FCSTD DOCUMENT
Label: SpoolCoaster
objects: Sketcher::SketchObject×1
note: 1 computed .brp shape members not serialized (recipe doc carries the construction recipe); baked Part::Feature solids carry a one-line shape summary decoded from their .brp

FEATURE [Sketcher::SketchObject] Sketch
  sketch-geometry (22):
    g0: Circle [constr] CenterX=0 CenterY=0 CenterZ=0 NormalX=0 NormalY=0 NormalZ=1 Radius=115
    g1: Circle [constr] CenterX=70 CenterY=-110 CenterZ=0 NormalX=0 NormalY=0 NormalZ=1 Radius=15
    g2: LineSegment StartX=-10 StartY=-117.726 StartZ=0 EndX=48.1322 EndY=-117.726 EndZ=0
    g3: LineSegment StartX=48.1322 StartY=-117.726 StartZ=0 EndX=62.9289 EndY=-102.929 EndZ=0
    g4: LineSegment StartX=80 StartY=-110 StartZ=0 EndX=80 EndY=-135 EndZ=0
    g5: ArcOfCircle CenterX=70 CenterY=-110 CenterZ=0 NormalX=0 NormalY=0 NormalZ=1 Radius=10 StartAngle=1.3058e-08 EndAngle=2.35619
    g6: LineSegment StartX=-5 StartY=-123.476 StartZ=0 EndX=60 EndY=-123.476 EndZ=0
    g7: LineSegment StartX=60 StartY=-123.476 StartZ=0 EndX=60 EndY=-126.976 EndZ=0
    g8: LineSegment StartX=60 StartY=-126.976 StartZ=0 EndX=-5 EndY=-126.976 EndZ=0
    g9: LineSegment StartX=-10 StartY=-117.726 StartZ=0 EndX=-10 EndY=-125.226 EndZ=0
    g10: LineSegment StartX=-10 StartY=-125.226 StartZ=0 EndX=-10 EndY=-132.726 EndZ=0
    g11: LineSegment StartX=-5 StartY=-123.476 StartZ=0 EndX=-5 EndY=-125.226 EndZ=0
    g12: LineSegment StartX=-5 StartY=-125.226 StartZ=0 EndX=-5 EndY=-126.976 EndZ=0
    g13: LineSegment [constr] StartX=-10 StartY=-125.226 StartZ=0 EndX=-5 EndY=-125.226 EndZ=0
    g14: Circle CenterX=70 CenterY=-110 CenterZ=0 NormalX=0 NormalY=0 NormalZ=1 Radius=1.8
    g15: Circle CenterX=75 CenterY=-135 CenterZ=0 NormalX=0 NormalY=0 NormalZ=1 Radius=1.8
    g16: LineSegment StartX=-10 StartY=-132.726 StartZ=0 EndX=48.1322 EndY=-132.726 EndZ=0
    g17: LineSegment StartX=48.1322 StartY=-132.726 StartZ=0 EndX=73.6617 EndY=-139.818 EndZ=0
    g18: ArcOfCircle CenterX=75 CenterY=-135 CenterZ=0 NormalX=0 NormalY=0 NormalZ=1 Radius=5 StartAngle=4.44143 EndAngle=6.28319
    g19: LineSegment [constr] StartX=48.1322 StartY=-117.726 StartZ=0 EndX=48.1322 EndY=-132.726 EndZ=0
    g20: Circle CenterX=75 CenterY=-128 CenterZ=0 NormalX=0 NormalY=0 NormalZ=1 Radius=1.8
    g21: LineSegment [constr] StartX=75 StartY=-128 StartZ=0 EndX=75 EndY=-135 EndZ=0
  constraints (64):
    c: DistanceX(g0) = 0
    c: DistanceY(g0) = 0
    c: DistanceX(g0) = 0
    c: DistanceY(g0) = 0
    c: Radius(g0) = 115
    c: DistanceX(g1) = 70
    c: DistanceY(g1) = -110
    c: Radius(g1) = 15
    c: Horizontal(g2)
    c: Coincident(g2,g3)
    c: Vertical(g4)
    c: Coincident(g5,g1)
    c: Coincident(g5,g3)
    c: Coincident(g5,g4)
    c: Tangent(g3,g5)
    c: Tangent(g4,g5)
    c: Radius(g5) = 10
    c: DistanceY(g1,g4) = -25
    c: Horizontal(g6)
    c: Coincident(g6,g7)
    c: Coincident(g7,g8)
    c: Horizontal(g8)
    c: Vertical(g7)
    c: DistanceX(g8) = -65
    c: Coincident(g9,g2)
    c: Vertical(g9)
    c: Coincident(g9,g10)
    c: Vertical(g10)
    c: Equal(g10,g9)
    c: Coincident(g11,g6)
    c: Vertical(g11)
    c: Coincident(g11,g12)
    c: Coincident(g12,g8)
    c: Vertical(g12)
    c: Equal(g12,g11)
    c: Coincident(g13,g9)
    c: Coincident(g13,g11)
    c: Horizontal(g13)
    c: DistanceY(g6,g8) = -3.5
    c: Coincident(g14,g1)
    c: Radius(g15) = 1.8
    c: Radius(g14) = 1.8
    c: Angle(g3) = 0.785398
    c: DistanceX(g10,g4) = 90
    c: Coincident(g16,g10)
    c: Horizontal(g16)
    c: Coincident(g16,g17)
    c: Tangent(g17,g0)
    c: Coincident(g18,g4)
    c: Coincident(g18,g17)
    c: Tangent(g18,g17)
    c: Tangent(g18,g4)
    c: Radius(g18) = 5
    c: DistanceY(g2,g10) = -15
    c: Coincident(g19,g2)
    c: Coincident(g19,g16)
    c: Vertical(g19)
    c: DistanceX(g8,g10) = -5
    c: Coincident(g15,g18)
    c: Equal(g20,g15)
    c: Coincident(g21,g20)
    c: Coincident(g21,g15)
    c: Vertical(g21)
    c: DistanceY(g21) = -7
